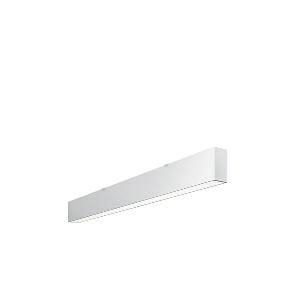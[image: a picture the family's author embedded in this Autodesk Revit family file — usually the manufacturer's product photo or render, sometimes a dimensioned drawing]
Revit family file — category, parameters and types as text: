
# Revit family: dotoo_line_-_dla_1500_830_d_end_00807942_3742
name_source: partatom
category: Lighting Fixtures
units: mm (PartAtom-declared; Revit-internal decimal feet)

## family parameters
Cut with Voids When Loaded = No
Host = Face
Light Source = No
Part Type = Normal
Room Calculation Point = No
Round Connector Dimension = Use Diameter
Shared = No

## types (1)
- DOTOO.line - DLA 1500/830/D END (1 x LED, 1300 lm, 3000K)
    Apparent Load = 13 VA
    Approval mark = CE
    CIE Flux Codes = 67 91 98 100 100
    Color Rendering = 80-89
    Color Temperature = 3000K
    Control Gear = Electronic ballast
    Default Elevation = 1800 mm
    Description = DLA 1500/830/D|Surface-mounted luminaire.|light source: LED|work equipment: Adjustable electronic ballast, digital DALI|connected load: 220-240 V, 50/60 Hz|Power consumption: approx. 13 W|luminous flux: 1300 lm|luminous efficacy: 100 lm/W|light distribution: Direct|colour temperature: Warm white, ca. 3000 K|class of protection: I|technology: Continuously dimmable|mains lead: Connector|glare control: Prism aperture|special features: DALI Load 1x, TouchDIM - dimming via standard switch, Through-wired, up to 18 m on one mains connection, Flicker-free, Suitable as emergency lighting, Mechanical and electrical connection of the individual modules without tools|
    Frequency = 50 Hz
    Height = 110 mm
    Lamp = 1 x LED
    Lamp Light Flux = 1300 lm
    Lamp count = 1
    Length = 1128 mm
    Luminous efficacy = 100 lm/W
    Manufacturer = Waldmann
    ModVariant = No
    Model = 00807942
    Mounting Place = Ceiling
    Mounting Type = Surface mounted
    Number of Poles = 1
    OnlyDefault = Yes
    Power Factor = 1
    Product Name = DOTOO.line - DLA 1500/830/D END
    Product group = Ceiling mounted luminaire
    ProductGroupID = 3
    Protection Class = Protection class I
    Protection Degree = IP 40
    RLX_Detail_Level = 1
    RLX_Emergency_Light_Flux = 0 lm
    RLX_Emergency_Type = 0
    RLX_Emergency_Type_DB = No
    RlxData = <blob elided: 15189 chars, md5=5c93f743>
    Socket = socket
    Standby Power = 0 W
    System Light Flux = 1300 lm
    System Power = 13 W
    Type Comments = Product without accessories
    Type Image = 114350000-00807927.jpg
    URL = http://relux.com
    VarID = ---
    Voltage = 230 V
    Voltage Range = 220-240 V
    Weight = 0.00 kg
    Width = 60 mm  [stored 0.19685 ft]

note: [stored X ft] marks values corroborated as IEEE doubles in the binary element streams (Revit-internal decimal feet)

## geometry (parser evidence)
native form markers: Sweep x12
no freeform markers — native parametric forms only
